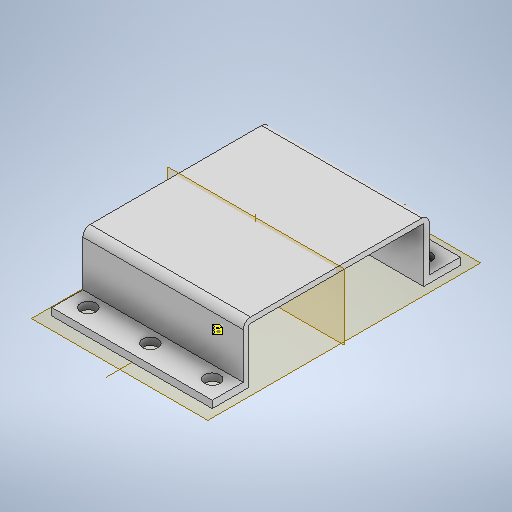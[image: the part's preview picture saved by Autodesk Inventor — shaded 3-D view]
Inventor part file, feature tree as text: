
AUTODESK INVENTOR PART (.ipt)
format: ipt  version: 2025 (Build 290162000, 162)  size: 266,240 bytes
history: native  units: mm
features: sketch x3, extrude x1, hole x1, mirror x1
ambient origin geometry x8: Origin, YZ Plane, XZ Plane, XY Plane, X Axis, Y Axis, Z Axis, Center Point
bodies: Solid1 (feature_tree)
feature tree (6):
  sketch  "Sketch1"  dims[d0=10.0mm d1=2.0mm]
  extrude  "Extrusion1"  Depth=2.0mm
  hole  "Hole1"  [1 undecoded]
  mirror  "Mirror1"
  sketch  "Sketch2"  dims[d2=8.5mm d4=15.0mm]
  sketch  "Sketch3"  dims[d5=24.0mm d6=1.5mm d7=2.0mm d8=44.0mm d9=0.0mm d10=5.0mm d12=17.0mm d14=5.0mm d15=4.2mm d16=6.0mm d17=4.0mm d18=2.0mm d19=90.0deg d20=8.0mm d21=20.594885mm d22=0.5mm d23=17.0mm d24=5.0mm]
note: 1 required parameter value undecoded (feature->parameter linkage not recoverable at this tier; creation-order binding heuristic only, values carry confidence <= 0.55)
